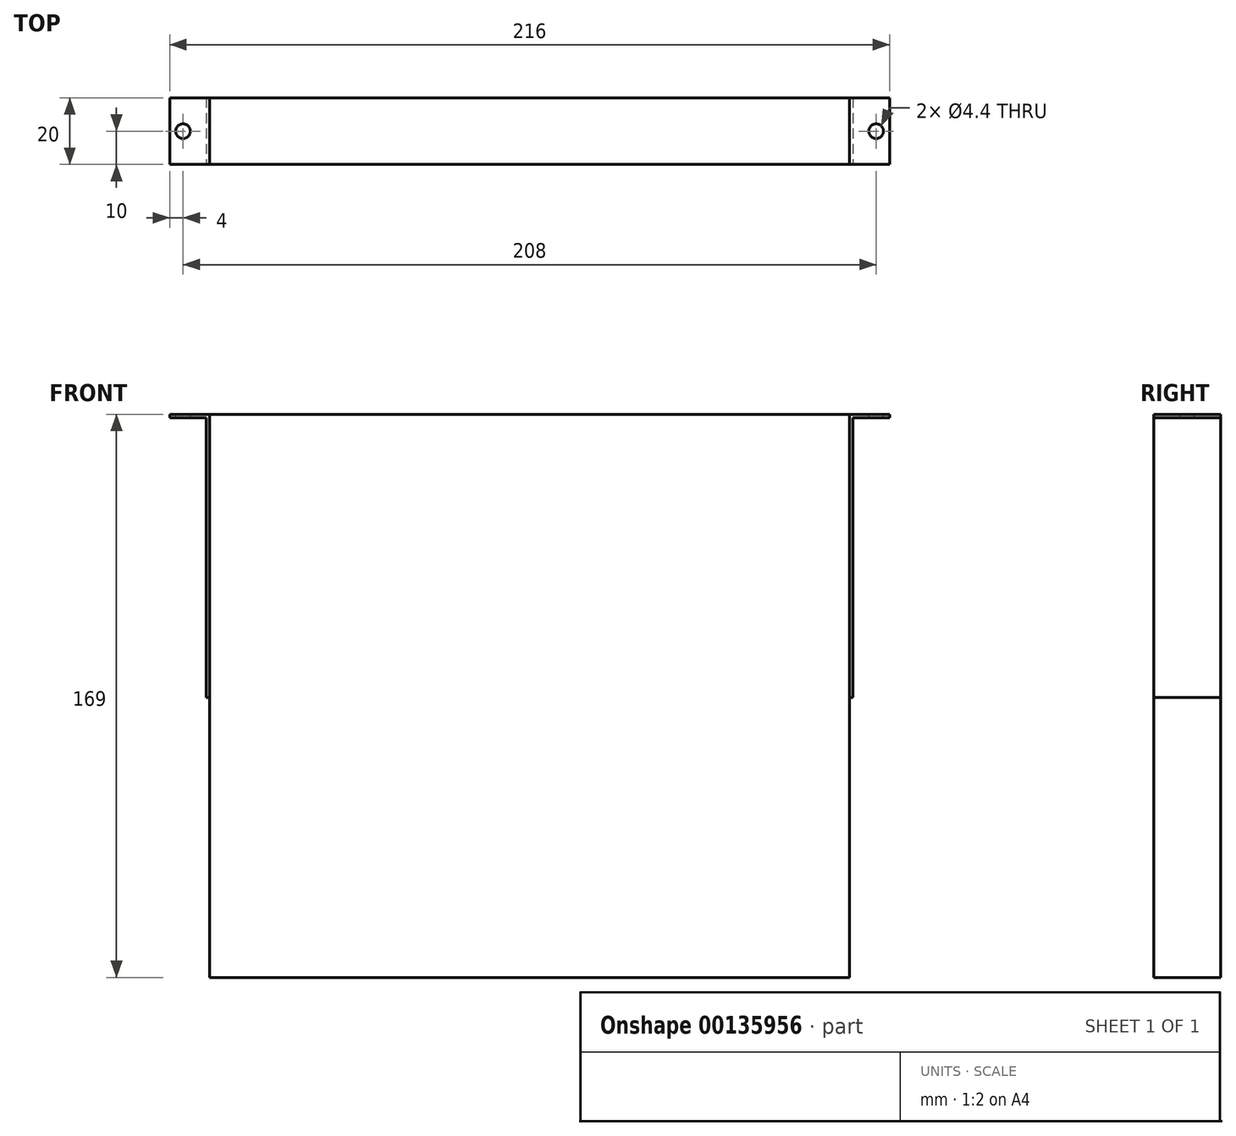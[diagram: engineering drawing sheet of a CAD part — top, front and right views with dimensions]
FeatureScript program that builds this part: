
annotation { "Feature Type Name" : "Feature", "Feature Type Description" : "" }
export const myFeature = defineFeature(function(context is Context, id is Id, definition is map)
    precondition{}
    {
        {
            var Q0;
            Q0=qCreatedBy(makeId("Front.planeOp"),FACE);
            var sketch = newSketch(context, id + "F0", { "sketchPlane" : qUnion([Q0])});
            skLineSegment(sketch, "E0.bottom", {"start": v(96, -84.5) * mm, "end": v(-96, -84.5) * mm});
            skLineSegment(sketch, "E0.top", {"start": v(96, 84.5) * mm, "end": v(-96, 84.5) * mm});
            skLineSegment(sketch, "E0.left", {"start": v(96, -84.5) * mm, "end": v(96, 84.5) * mm});
            skLineSegment(sketch, "E0.right", {"start": v(-96, -84.5) * mm, "end": v(-96, 84.5) * mm});
            skPoint(sketch, "E0.middle", {"position": v(0, 0) * mm});
            skSolve(sketch);
        }
        {
            var Q0;
            Q0 = qSketchRegion(id + "F0", true);
            extrude(context, id + "F1", {"entities" : qUnion([Q0]), "depth" : 20 * mm});
        }
        {
            var Q0;
            Q0=makeQuery(id+"F1.opExtrude","CAP_FACE",FACE,{"disambiguationData":[OSD([sQuery(id+"F0.wireOp",EDGE,"E0.bottom"),sQuery(id+"F0.wireOp",EDGE,"E0.top"),sQuery(id+"F0.wireOp",EDGE,"E0.left"),sQuery(id+"F0.wireOp",EDGE,"E0.right")])],"isStart":false});
            var sketch = newSketch(context, id + "F2", { "sketchPlane" : qUnion([Q0])});
            skLineSegment(sketch, "E1.bottom", {"start": v(-96, 84.5) * mm, "end": v(-97, 84.5) * mm});
            skLineSegment(sketch, "E1.top", {"start": v(-96, -0.5) * mm, "end": v(-97, -0.5) * mm});
            skLineSegment(sketch, "E1.left", {"start": v(-96, 84.5) * mm, "end": v(-96, -0.5) * mm});
            skLineSegment(sketch, "E1.right", {"start": v(-97, 83.5) * mm, "end": v(-97, -0.5) * mm});
            skLineSegment(sketch, "E2.bottom", {"start": v(-97, 84.5) * mm, "end": v(-108, 84.5) * mm});
            skLineSegment(sketch, "E2.top", {"start": v(-97, 83.5) * mm, "end": v(-108, 83.5) * mm});
            skLineSegment(sketch, "E2.right", {"start": v(-108, 84.5) * mm, "end": v(-108, 83.5) * mm});
            skLineSegment(sketch, "E3.MirrorCS", {"start": v(108, 84.5) * mm, "end": v(108, 83.5) * mm});
            skLineSegment(sketch, "E4.MirrorCS", {"start": v(97, 84.5) * mm, "end": v(108, 84.5) * mm});
            skLineSegment(sketch, "E5.MirrorCS", {"start": v(97, 83.5) * mm, "end": v(108, 83.5) * mm});
            skLineSegment(sketch, "E6.MirrorCS", {"start": v(96, 84.5) * mm, "end": v(97, 84.5) * mm});
            skLineSegment(sketch, "E7.MirrorCS", {"start": v(96, 84.5) * mm, "end": v(96, -0.5) * mm});
            skLineSegment(sketch, "E8.MirrorCS", {"start": v(97, 83.5) * mm, "end": v(97, -0.5) * mm});
            skLineSegment(sketch, "E9.MirrorCS", {"start": v(96, -0.5) * mm, "end": v(97, -0.5) * mm});
            skSolve(sketch);
        }
        {
            var Q0;
            Q0 = qSketchRegion(id + "F2", true);
            extrude(context, id + "F3", {"entities" : qUnion([Q0]), "oppositeDirection" : true, "depth" : 20 * mm});
        }
        {
            var Q0;
            Q0=makeQuery(id+"F3.opExtrude","SWEPT_FACE",FACE,{"disambiguationData":[OSD([sQuery(id+"F2.wireOp",EDGE,"E1.bottom"),sQuery(id+"F2.wireOp",EDGE,"E2.bottom")])]});
            var sketch = newSketch(context, id + "F4", { "sketchPlane" : qUnion([Q0])});
            skCircle(sketch, "E10", {"center": v(-104, -10) * mm, "radius": 2 * mm});
            skCircle(sketch, "E11.MirrorC", {"center": v(104, -10) * mm, "radius": 2 * mm});
            skSolve(sketch);
        }
        {
            var Q0;
            Q0=sQuery(id+"F4.wireOp",VERTEX,"E10.center");
            var Q1;
            Q1=sQuery(id+"F4.wireOp",VERTEX,"E11.MirrorC.center");
            var Q2;
            Q2=makeQuery(id+"F3.opExtrude","SWEPT_BODY",BODY,{"disambiguationData":[OSD([sQuery(id+"F2.wireOp",EDGE,"E1.bottom"),sQuery(id+"F2.wireOp",EDGE,"E1.top"),sQuery(id+"F2.wireOp",EDGE,"E1.left"),sQuery(id+"F2.wireOp",EDGE,"E1.right"),sQuery(id+"F2.wireOp",EDGE,"E2.bottom"),sQuery(id+"F2.wireOp",EDGE,"E2.top"),sQuery(id+"F2.wireOp",EDGE,"E2.right")])]});
            var Q3;
            Q3=makeQuery(id+"F3.opExtrude","SWEPT_BODY",BODY,{"disambiguationData":[OSD([sQuery(id+"F2.wireOp",EDGE,"E3.MirrorCS"),sQuery(id+"F2.wireOp",EDGE,"E4.MirrorCS"),sQuery(id+"F2.wireOp",EDGE,"E5.MirrorCS"),sQuery(id+"F2.wireOp",EDGE,"E6.MirrorCS"),sQuery(id+"F2.wireOp",EDGE,"E7.MirrorCS"),sQuery(id+"F2.wireOp",EDGE,"E8.MirrorCS"),sQuery(id+"F2.wireOp",EDGE,"E9.MirrorCS")])]});
            hole(context, id + "F5", {"style" : HoleStyle.SIMPLE, "endStyle" : HoleEndStyle.BLIND, "standardTappedOrClearance" : lookupTablePath({ "standard" : "ISO", "fit" : "Normal", "size" : "M4", "type" : "Clearance" }), "standardBlindInLast" : lookupTablePath({ "fit" : "Standard", "standard" : "ISO", "size" : "M4", "type" : "Clearance" }), "holeDiameter" : 4.4 * mm, "holeDepth" : 12 * mm, "startFromSketch" : true, "locations" : qUnion([Q0, Q1]), "scope" : qUnion([Q2, Q3])});
        }
    });
